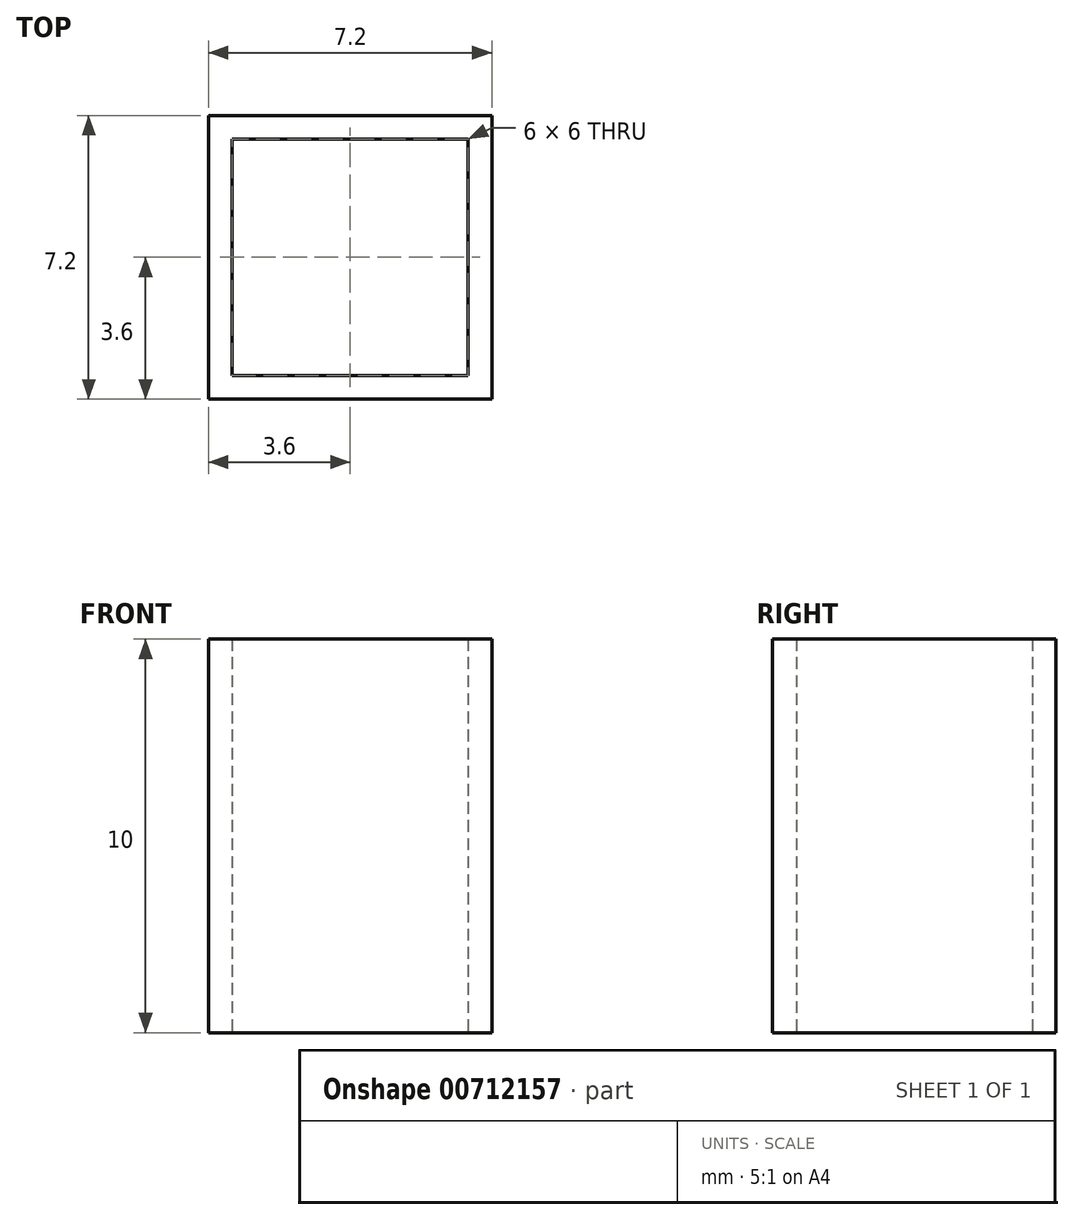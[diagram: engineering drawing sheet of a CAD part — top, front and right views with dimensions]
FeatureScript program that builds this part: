
annotation { "Feature Type Name" : "Feature", "Feature Type Description" : "" }
export const myFeature = defineFeature(function(context is Context, id is Id, definition is map)
    precondition{}
    {
        {
            var Q0;
            Q0=qCreatedBy(makeId("Top.planeOp"),FACE);
            var sketch = newSketch(context, id + "F0", { "sketchPlane" : qUnion([Q0])});
            skLineSegment(sketch, "E0.bottom", {"start": v(3.6, 3.6) * mm, "end": v(-3.6, 3.6) * mm});
            skLineSegment(sketch, "E0.top", {"start": v(3.6, -3.6) * mm, "end": v(-3.6, -3.6) * mm});
            skLineSegment(sketch, "E0.left", {"start": v(3.6, 3.6) * mm, "end": v(3.6, -3.6) * mm});
            skLineSegment(sketch, "E0.right", {"start": v(-3.6, 3.6) * mm, "end": v(-3.6, -3.6) * mm});
            skPoint(sketch, "E0.middle", {"position": v(0, 0) * mm});
            skLineSegment(sketch, "E1.bottom", {"start": v(3, 3) * mm, "end": v(-3, 3) * mm});
            skLineSegment(sketch, "E1.top", {"start": v(3, -3) * mm, "end": v(-3, -3) * mm});
            skLineSegment(sketch, "E1.left", {"start": v(3, 3) * mm, "end": v(3, -3) * mm});
            skLineSegment(sketch, "E1.right", {"start": v(-3, 3) * mm, "end": v(-3, -3) * mm});
            skSolve(sketch);
        }
        {
            var Q0;
            Q0=makeQuery(id+"F0.imprint","IMPRINT",FACE,{"disambiguationData":[TD([[makeQuery(id+"F0.imprint","IMPRINT",EDGE,{"derivedFrom":sQuery(id+"F0.wireOp",EDGE,"E0.bottom")}),1.0]])]});
            extrude(context, id + "F1", {"entities" : qUnion([Q0]), "depth" : 10 * mm, "offsetDistance" : 25 * mm});
        }
    });
